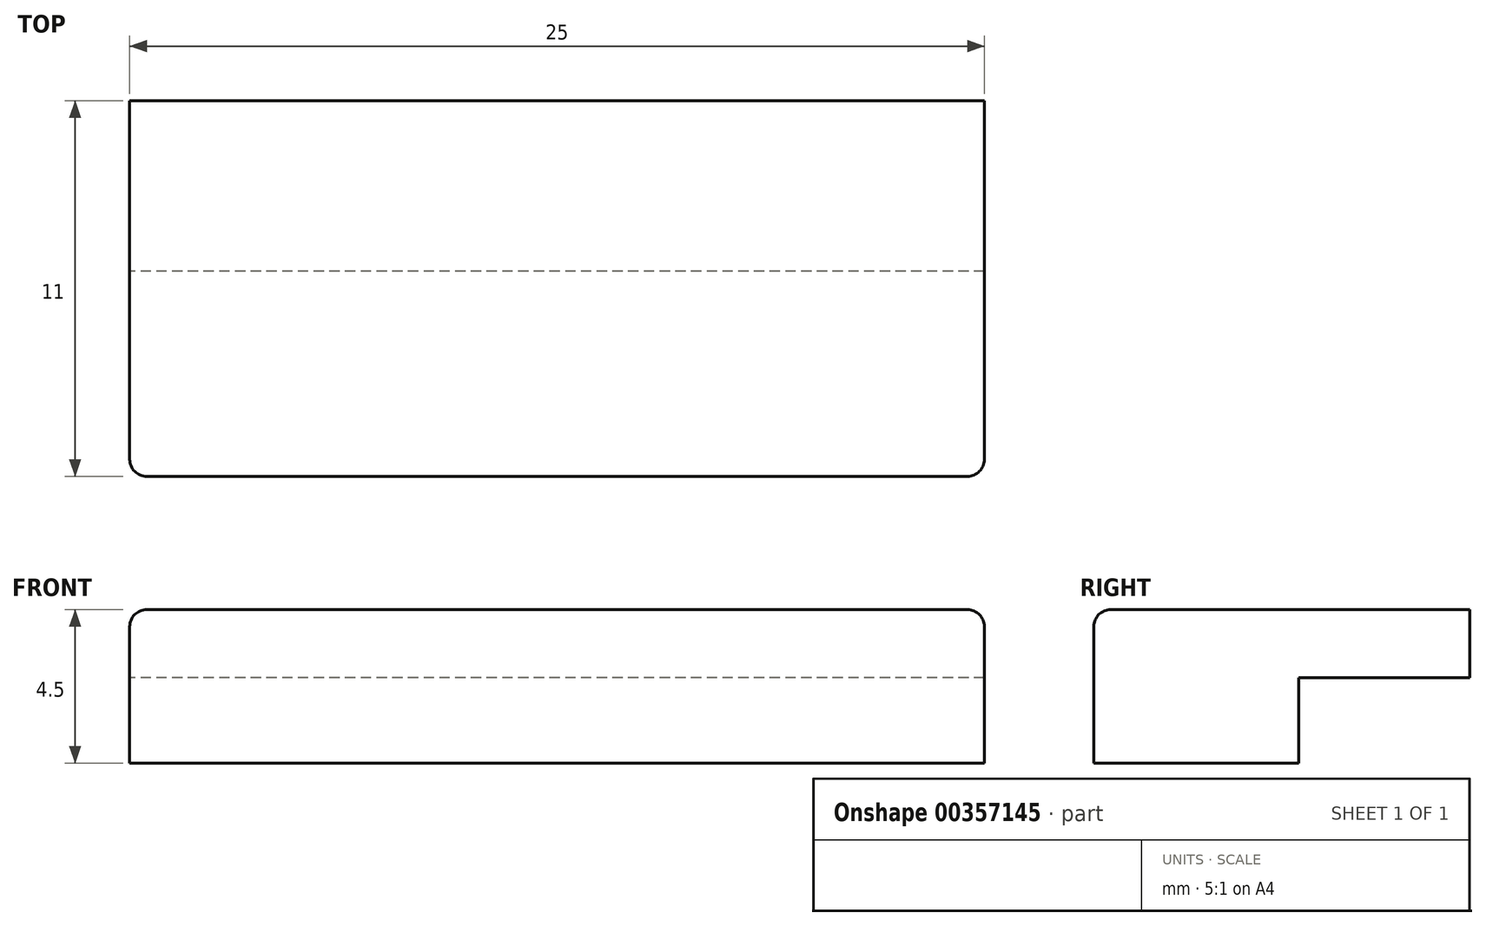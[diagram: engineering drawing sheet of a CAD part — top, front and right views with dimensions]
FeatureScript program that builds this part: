
annotation { "Feature Type Name" : "Feature", "Feature Type Description" : "" }
export const myFeature = defineFeature(function(context is Context, id is Id, definition is map)
    precondition{}
    {
        {
            var Q0;
            Q0=qCreatedBy(makeId("Top.planeOp"),FACE);
            var sketch = newSketch(context, id + "F0", { "sketchPlane" : qUnion([Q0])});
            skLineSegment(sketch, "E0.bottom", {"start": v(12.5, 3) * mm, "end": v(-12.5, 3) * mm});
            skLineSegment(sketch, "E0.top", {"start": v(12.5, -3) * mm, "end": v(-12.5, -3) * mm});
            skLineSegment(sketch, "E0.left", {"start": v(12.5, 3) * mm, "end": v(12.5, -3) * mm});
            skLineSegment(sketch, "E0.right", {"start": v(-12.5, 3) * mm, "end": v(-12.5, -3) * mm});
            skPoint(sketch, "E0.middle", {"position": v(0, 0) * mm});
            skSolve(sketch);
        }
        {
            var Q0;
            Q0 = qSketchRegion(id + "F0", true);
            extrude(context, id + "F1", {"entities" : qUnion([Q0]), "depth" : 4.5 * mm});
        }
        {
            var Q0;
            Q0=makeQuery(id+"F1.opExtrude","SWEPT_FACE",FACE,{"disambiguationData":[OSD([sQuery(id+"F0.wireOp",EDGE,"E0.bottom")])]});
            var sketch = newSketch(context, id + "F2", { "sketchPlane" : qUnion([Q0])});
            skLineSegment(sketch, "E1.top", {"start": v(-12.5, 2.5) * mm, "end": v(10.17, 2.5) * mm});
            skLineSegment(sketch, "E2.bottom", {"start": v(-12.5, 4.5) * mm, "end": v(12.5, 4.5) * mm});
            skLineSegment(sketch, "E2.top", {"start": v(-12.5, 2.5) * mm, "end": v(12.5, 2.5) * mm});
            skLineSegment(sketch, "E2.left", {"start": v(-12.5, 4.5) * mm, "end": v(-12.5, 2.5) * mm});
            skLineSegment(sketch, "E2.right", {"start": v(12.5, 4.5) * mm, "end": v(12.5, 2.5) * mm});
            skSolve(sketch);
        }
        {
            var Q0;
            Q0 = qSketchRegion(id + "F2", true);
            extrude(context, id + "F3", {"entities" : qUnion([Q0]), "operationType" : NewBodyOperationType.ADD, "depth" : 5 * mm});
        }
        {
            var Q0;
            Q0=makeQuery(id+"F1.opExtrude","CAP_EDGE",EDGE,{"disambiguationData":[OSD([sQuery(id+"F0.wireOp",EDGE,"E0.top")])],"isStart":false});
            fillet(context, id + "F4", {"entities" : qUnion([Q0]), "radius" : .5 * mm, "tangentPropagation" : true, "allowEdgeOverflow" : false});
        }
        {
            var Q0;
            Q0=makeQuery(id+"F3.boolean.opBoolean","MERGE",EDGE,{"derivedFrom":[makeQuery(id+"F1.opExtrude","CAP_EDGE",EDGE,{"disambiguationData":[OSD([sQuery(id+"F0.wireOp",EDGE,"E0.left")])],"isStart":false}),makeQuery(id+"F3.opExtrude","SWEPT_EDGE",EDGE,{"disambiguationData":[OSD([sQuery(id+"F2.wireOp",EDGE,"E2.bottom"),sQuery(id+"F2.wireOp",EDGE,"E2.left")])]})]});
            var Q1;
            Q1=makeQuery(id+"F3.boolean.opBoolean","MERGE",EDGE,{"derivedFrom":[makeQuery(id+"F1.opExtrude","CAP_EDGE",EDGE,{"disambiguationData":[OSD([sQuery(id+"F0.wireOp",EDGE,"E0.right")])],"isStart":false}),makeQuery(id+"F3.opExtrude","SWEPT_EDGE",EDGE,{"disambiguationData":[OSD([sQuery(id+"F2.wireOp",EDGE,"E2.bottom"),sQuery(id+"F2.wireOp",EDGE,"E2.right")])]})]});
            fillet(context, id + "F5", {"entities" : qUnion([Q0, Q1]), "radius" : .5 * mm, "tangentPropagation" : true, "allowEdgeOverflow" : false});
        }
    });
